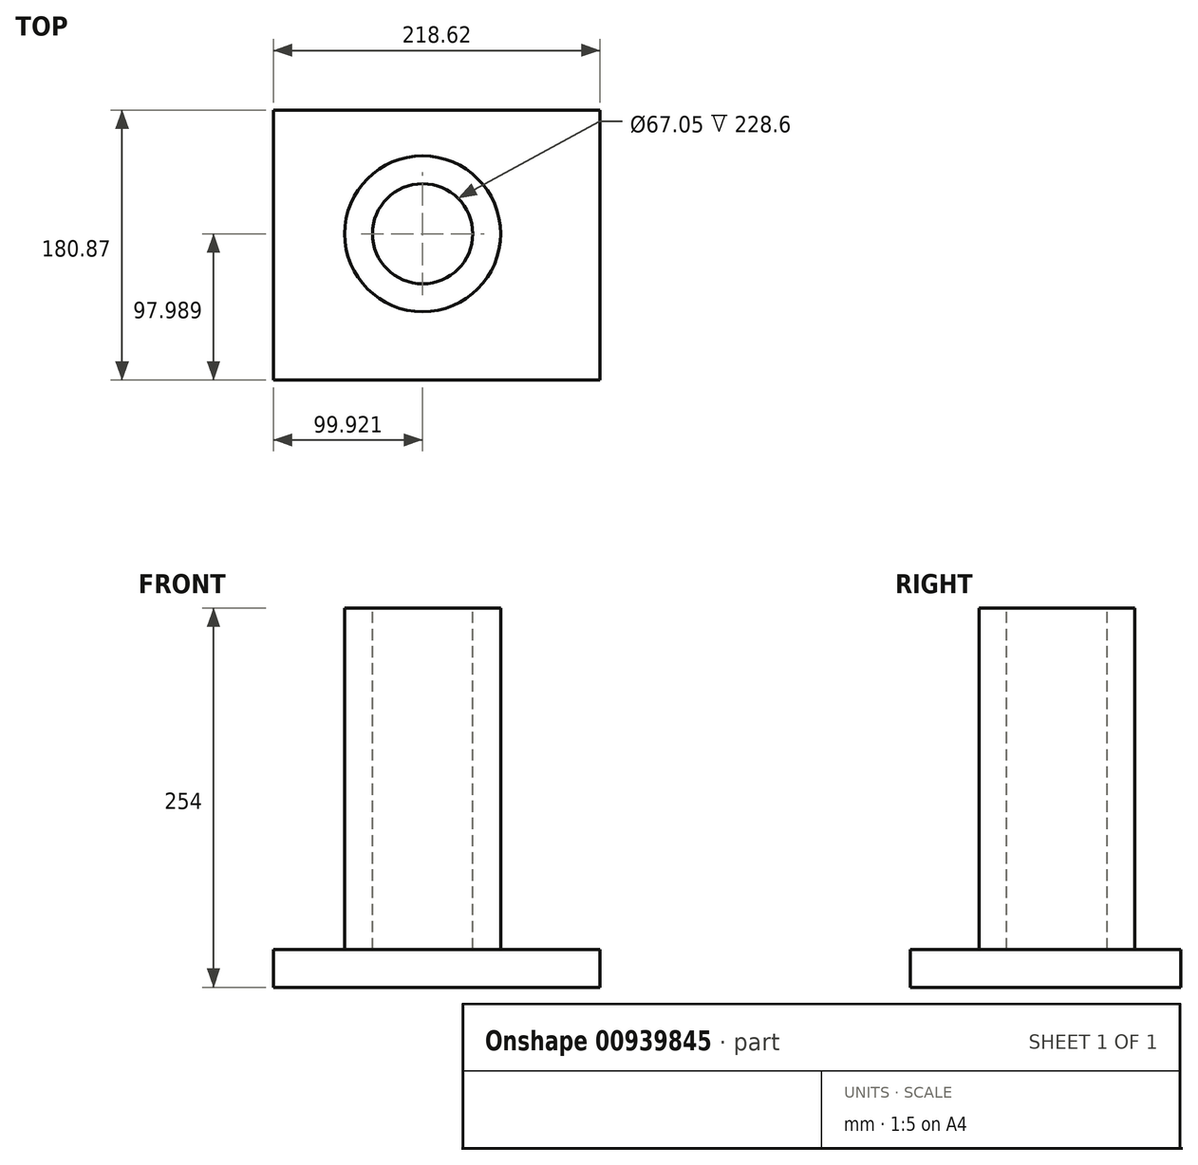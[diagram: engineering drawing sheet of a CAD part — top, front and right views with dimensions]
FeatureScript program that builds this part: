
annotation { "Feature Type Name" : "Feature", "Feature Type Description" : "" }
export const myFeature = defineFeature(function(context is Context, id is Id, definition is map)
    precondition{}
    {
        {
            var Q0;
            Q0=qCreatedBy(makeId("Top.planeOp"),FACE);
            var sketch = newSketch(context, id + "F0", { "sketchPlane" : qUnion([Q0])});
            skCircle(sketch, "E0", {"center": v(5.62, -5.62) * mm, "radius": 52.14 * mm});
            skSolve(sketch);
        }
        {
            var Q0;
            Q0=makeQuery(id+"F0.imprint","IMPRINT",FACE,{"disambiguationData":[TD([[makeQuery(id+"F0.imprint","IMPRINT",EDGE,{"derivedFrom":sQuery(id+"F0.wireOp",EDGE,"E0")}),1.0]])]});
            extrude(context, id + "F1", {"entities" : qUnion([Q0]), "depth" : 254 * mm, "offsetDistance" : 25.4 * mm});
        }
        {
            var Q0;
            Q0=makeQuery(id+"F1.opExtrude","CAP_FACE",FACE,{"disambiguationData":[OSD([sQuery(id+"F0.wireOp",EDGE,"E0")])],"isStart":false});
            var sketch = newSketch(context, id + "F2", { "sketchPlane" : qUnion([Q0])});
            skCircle(sketch, "E1", {"center": v(5.62, -5.62) * mm, "radius": 33.53 * mm});
            skSolve(sketch);
        }
        {
            var Q0;
            Q0 = qSketchRegion(id + "F2", true);
            extrude(context, id + "F3", {"entities" : qUnion([Q0]), "operationType" : NewBodyOperationType.REMOVE, "endBound" : BoundingType.THROUGH_ALL, "oppositeDirection" : true, "depth" : 25.4 * mm, "offsetDistance" : 25.4 * mm});
        }
        {
            var Q0;
            Q0=qCreatedBy(makeId("Top.planeOp"),FACE);
            var sketch = newSketch(context, id + "F4", { "sketchPlane" : qUnion([Q0])});
            skLineSegment(sketch, "E2.bottom", {"start": v(-94.3, 77.26) * mm, "end": v(124.32, 77.26) * mm});
            skLineSegment(sketch, "E2.top", {"start": v(-94.3, -103.61) * mm, "end": v(124.32, -103.61) * mm});
            skLineSegment(sketch, "E2.left", {"start": v(-94.3, 77.26) * mm, "end": v(-94.3, -103.61) * mm});
            skLineSegment(sketch, "E2.right", {"start": v(124.32, 77.26) * mm, "end": v(124.32, -103.61) * mm});
            skSolve(sketch);
        }
        {
            var Q0;
            Q0 = qSketchRegion(id + "F4", true);
            extrude(context, id + "F5", {"entities" : qUnion([Q0]), "operationType" : NewBodyOperationType.ADD, "depth" : 25.4 * mm, "offsetDistance" : 25.4 * mm});
        }
    });
